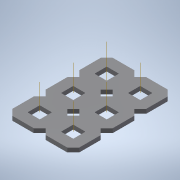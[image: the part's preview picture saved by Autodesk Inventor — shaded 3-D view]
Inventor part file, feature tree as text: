
AUTODESK INVENTOR PART (.ipt)
format: ipt  version: 2020 (Build 240168000, 168)  size: 1,136,640 bytes
history: native  units: in
note: dims shown in document units (in); Inventor stores cm internally (conversion verified against a paired STEP export)
features: other x15, extrude x2, plane x2, split x2, pattern_linear x1, imported_body x1
ambient origin geometry x8: Origin, YZ Plane, XZ Plane, XY Plane, X Axis, Y Axis, Z Axis, Center Point
bodies: Body1 (feature_tree)
feature tree (23):
  other  "Diamond-Pattern"
  other  "Plate"
  extrude  "length cut"  TaperAngle=0.0deg  [1 undecoded]
  extrude  "width cut"  TaperAngle=0.0deg  [1 undecoded]
  other  "constraint axis"
  pattern_linear  "constraint axes"  Spacing1=0.5in  [1 undecoded]
  other  "front plane"
  other  "right plane"
  plane  "Work Plane5"
  split  "Split1"
  plane  "Work Plane6"
  split  "Split2"
  imported_body  "Base1"
  other  "length profile"
  other  "width profile"
  other  "Work Point1"
  other  "Work Axis36"
  other  "Work Axis40"
  other  "Work Axis42"
  other  "back plane"
  other  "left plane"
  other  "Work Axis170"
  other  "Work Axis171"
note: 3 required parameter values undecoded (feature->parameter linkage not recoverable at this tier; creation-order binding heuristic only, values carry confidence <= 0.55)
